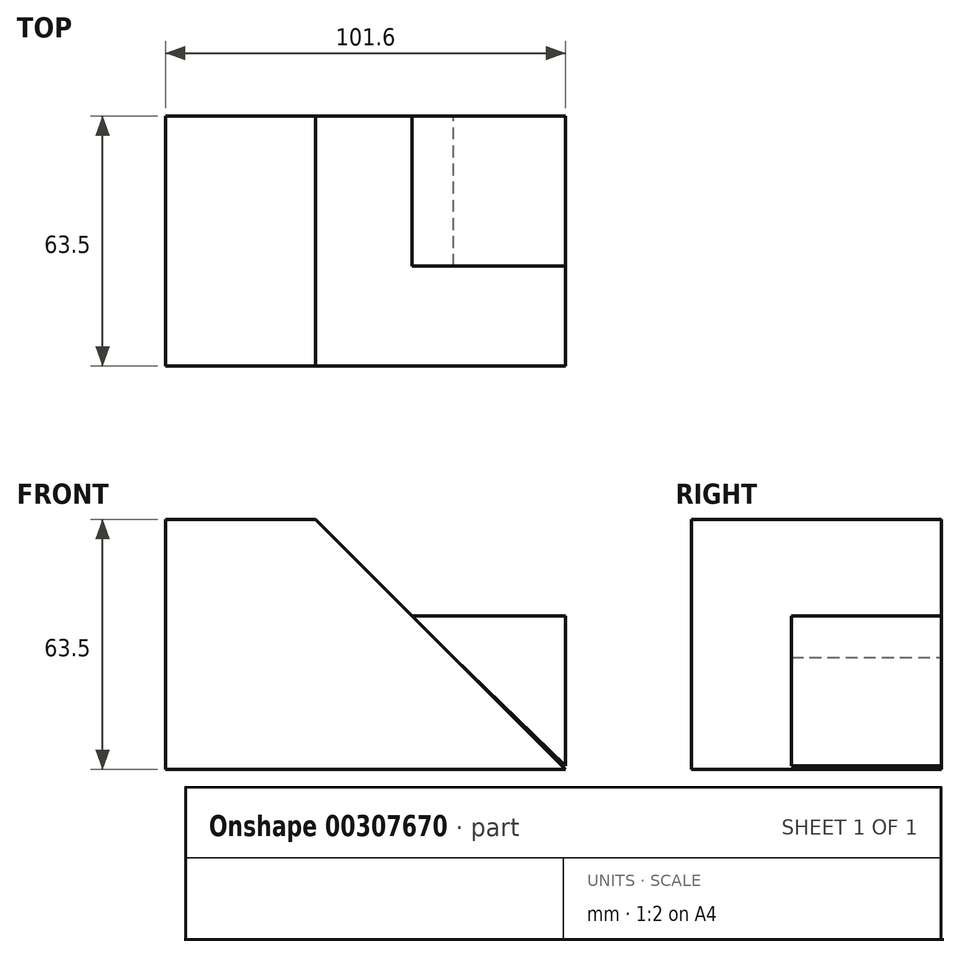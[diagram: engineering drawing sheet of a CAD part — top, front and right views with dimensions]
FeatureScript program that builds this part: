
annotation { "Feature Type Name" : "Feature", "Feature Type Description" : "" }
export const myFeature = defineFeature(function(context is Context, id is Id, definition is map)
    precondition{}
    {
        {
            var Q0;
            Q0=qCreatedBy(makeId("Front.planeOp"),FACE);
            var sketch = newSketch(context, id + "F0", { "sketchPlane" : qUnion([Q0])});
            skLineSegment(sketch, "E0", {"start": v(-47.5, -29.86) * mm, "end": v(54.1, -29.86) * mm});
            skLineSegment(sketch, "E1", {"start": v(54.1, -29.86) * mm, "end": v(-9.4, 33.64) * mm});
            skLineSegment(sketch, "E2", {"start": v(-9.4, 33.64) * mm, "end": v(-47.5, 33.64) * mm});
            skLineSegment(sketch, "E3", {"start": v(-47.5, 33.64) * mm, "end": v(-47.5, -29.86) * mm});
            skSolve(sketch);
        }
        {
            var Q0;
            Q0=makeQuery(id+"F0.imprint","IMPRINT",FACE,{"disambiguationData":[TD([[makeQuery(id+"F0.imprint","IMPRINT",EDGE,{"derivedFrom":sQuery(id+"F0.wireOp",EDGE,"E0")}),1.0]])]});
            extrude(context, id + "F1", {"entities" : qUnion([Q0]), "depth" : 63.5 * mm});
        }
        {
            var Q0;
            Q0=qCreatedBy(makeId("Front.planeOp"),FACE);
            var sketch = newSketch(context, id + "F2", { "sketchPlane" : qUnion([Q0])});
            skLineSegment(sketch, "E4", {"start": v(54.06, -28.96) * mm, "end": v(54.06, 9.09) * mm});
            skLineSegment(sketch, "E5", {"start": v(54.06, 9.09) * mm, "end": v(14.83, 9.09) * mm});
            skLineSegment(sketch, "E6", {"start": v(14.83, 9.09) * mm, "end": v(54.06, -28.96) * mm});
            skSolve(sketch);
        }
        {
            var Q0;
            Q0=makeQuery(id+"F2.imprint","IMPRINT",FACE,{"disambiguationData":[TD([[makeQuery(id+"F2.imprint","IMPRINT",EDGE,{"derivedFrom":sQuery(id+"F2.wireOp",EDGE,"E4")}),1.0]])]});
            extrude(context, id + "F3", {"entities" : qUnion([Q0]), "operationType" : NewBodyOperationType.ADD, "depth" : 38.1 * mm});
        }
    });
